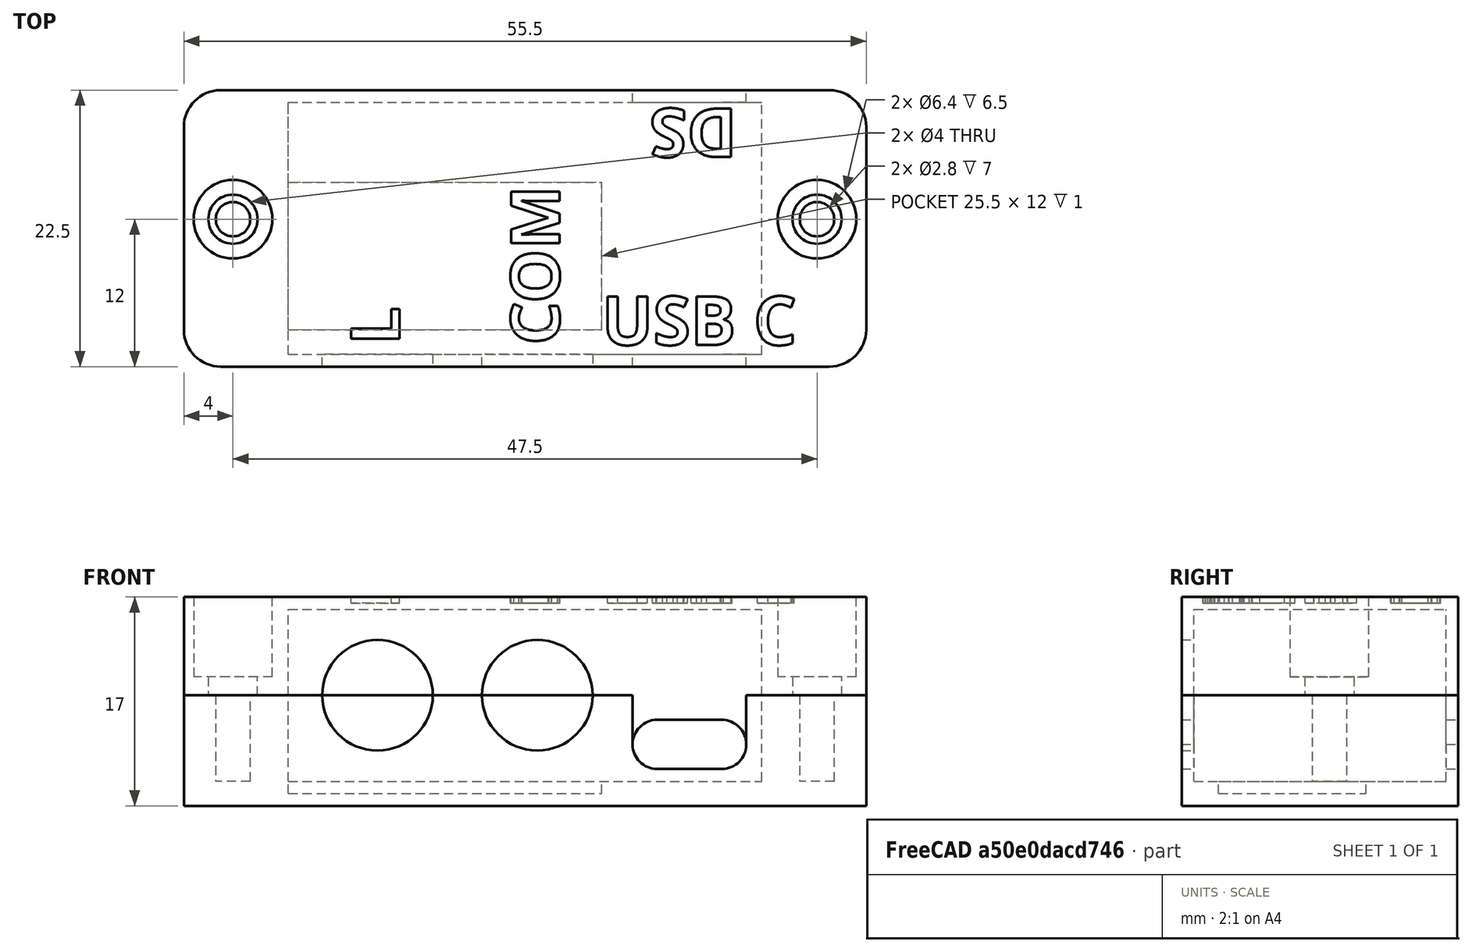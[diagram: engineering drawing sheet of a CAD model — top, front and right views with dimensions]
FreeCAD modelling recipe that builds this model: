
FCSTD DOCUMENT  (FreeCAD 0.21R33771 (Git))
Label: ds_lite_macro_tv_out_box
License: All rights reserved
LicenseURL: https://en.wikipedia.org/wiki/All_rights_reserved
objects: Part::Box×11, Part::Cylinder×10, Part::Fillet×6, Part::Cut×6, Part::MultiFuse×5, Part::Part2DObjectPython×4, Part::Extrusion×4
note: 46 computed .brp shape members not serialized (recipe doc carries the construction recipe); baked Part::Feature solids carry a one-line shape summary decoded from their .brp

FEATURE [Part::Box] Box  label="Cube(inner_base)"
  AttacherType = Attacher::AttachEngine3D
  Height = 7
  Length = 38.5
  Width = 20.5
FEATURE [Part::Box] Box001  label="Cube001(usb_c_charging)"
  AttacherType = Attacher::AttachEngine3D
  Height = 7
  Length = 9.25
  Placement = pos=(28,-1,1) rot=(0,0,1;0rad)
  Width = 1
FEATURE [Part::Cylinder] Cylinder  label="Cylinder(com_port_base)"
  Angle = 360
  AttacherType = Attacher::AttachEngine3D
  FirstAngle = 0
  Height = 1
  Placement = pos=(20.25,0,7) rot=(1,0,0;1.5708rad)
  Radius = 4.5
  SecondAngle = 0
FEATURE [Part::Box] Box002  label="Cube(outer_base)"
  AttacherType = Attacher::AttachEngine3D
  Height = 9
  Length = 55.5
  Placement = pos=(-8.5,-1,-2) rot=(0,0,1;0rad)
  Width = 22.5
FEATURE [Part::Cylinder] Cylinder001  label="Cylinder(L_port_base)"
  Angle = 360
  AttacherType = Attacher::AttachEngine3D
  FirstAngle = 0
  Height = 1
  Placement = pos=(7.25,0,7) rot=(1,0,0;1.5708rad)
  Radius = 4.5
  SecondAngle = 0
FEATURE [Part::Box] Box003  label="Cube001(usb_c_ds_side)"
  AttacherType = Attacher::AttachEngine3D
  Height = 7
  Length = 9.25
  Placement = pos=(28,20.5,1) rot=(0,0,1;0rad)
  Width = 1
FEATURE [Part::Fillet] Fillet  label="Fillet(usb_c_charging_base)"
  Base = -> Box001
  Edges = 2 edges r=2: [Edge4,Edge8]
FEATURE [Part::Fillet] Fillet001  label="Fillet001(usb_c_ds_side_base)"
  Base = -> Box003
  Edges = 2 edges r=2: [Edge4,Edge8]
FEATURE [Part::Box] Box004  label="Cube(inner_lid)"
  AttacherType = Attacher::AttachEngine3D
  Height = 7
  Length = 38.5
  Placement = pos=(0,0,7) rot=(0,0,1;0rad)
  Width = 20.5
FEATURE [Part::Box] Box005  label="Cube(outer_lid)"
  AttacherType = Attacher::AttachEngine3D
  Height = 8
  Length = 55.5
  Placement = pos=(-8.5,-1,7) rot=(0,0,1;0rad)
  Width = 22.5
FEATURE [Part::Box] Box006  label="Cube(inner_base_cutout)"
  AttacherType = Attacher::AttachEngine3D
  Height = 1
  Length = 25.5
  Placement = pos=(0,2,-1) rot=(0,0,1;0rad)
  Width = 12
FEATURE [Part::Box] Box007  label="Cube001(usb_c_charging_lid)"
  AttacherType = Attacher::AttachEngine3D
  Height = 4.5
  Length = 9.25
  Placement = pos=(28,-1,2.5) rot=(0,0,1;0rad)
  Width = 1
FEATURE [Part::Box] Box008  label="Cube001(usb_c_ds_side_lid)"
  AttacherType = Attacher::AttachEngine3D
  Height = 4.5
  Length = 9.25
  Placement = pos=(28,20.5,2.5) rot=(0,0,1;0rad)
  Width = 1
FEATURE [Part::Cylinder] Cylinder002  label="Cylinder(L_port_lid)"
  Angle = 360
  AttacherType = Attacher::AttachEngine3D
  FirstAngle = 0
  Height = 1
  Placement = pos=(7.25,0,7) rot=(1,0,0;1.5708rad)
  Radius = 4.5
  SecondAngle = 0
FEATURE [Part::Cylinder] Cylinder003  label="Cylinder(com_port_lid)"
  Angle = 360
  AttacherType = Attacher::AttachEngine3D
  FirstAngle = 0
  Height = 1
  Placement = pos=(20.25,0,7) rot=(1,0,0;1.5708rad)
  Radius = 4.5
  SecondAngle = 0
FEATURE [Part::MultiFuse] Fusion
  Shapes = -> [Box,Cylinder,Cylinder001,Fillet,Fillet001,Box006]
FEATURE [Part::Cut] Cut  label="Cut(base)"
  Base = -> Box002
  Tool = -> Fusion
FEATURE [Part::Box] Box009  label="Cube001(usb_c_charging_lid)001"
  AttacherType = Attacher::AttachEngine3D
  Height = 2.5
  Length = 9.25
  Placement = pos=(28,-1,2.5) rot=(0,0,1;0rad)
  Width = 1
FEATURE [Part::Fillet] Fillet002
  Base = -> Box009
  Edges = 2 edges r=2: [Edge2,Edge6]
FEATURE [Part::Cut] Cut001
  Base = -> Box007
  Tool = -> Fillet002
FEATURE [Part::Box] Box010  label="Cube001(usb_c_ds_side_lid)001"
  AttacherType = Attacher::AttachEngine3D
  Height = 2.5
  Length = 9.25
  Placement = pos=(28,20.5,2.5) rot=(0,0,1;0rad)
  Width = 1
FEATURE [Part::Fillet] Fillet003
  Base = -> Box010
  Edges = 2 edges r=2: [Edge2,Edge6]
FEATURE [Part::Cut] Cut002
  Base = -> Box008
  Tool = -> Fillet003
FEATURE [Part::Cylinder] Cylinder004  label="Cylinder(bolt_head_clear_left)"
  Angle = 360
  AttacherType = Attacher::AttachEngine3D
  FirstAngle = 0
  Height = 6.5
  Placement = pos=(-4.5,11,8.5) rot=(0,0,1;0rad)
  Radius = 3.2
  SecondAngle = 0
FEATURE [Part::Cylinder] Cylinder005  label="Cylinder(bolt_thread_left)"
  Angle = 360
  AttacherType = Attacher::AttachEngine3D
  FirstAngle = 0
  Height = 7
  Placement = pos=(-4.5,11,0) rot=(0,0,1;0rad)
  Radius = 1.4
  SecondAngle = 0
FEATURE [Part::Cylinder] Cylinder006  label="Cylinder(bolt_clear_left)"
  Angle = 360
  AttacherType = Attacher::AttachEngine3D
  FirstAngle = 0
  Height = 1.5
  Placement = pos=(-4.5,11,7) rot=(0,0,1;0rad)
  Radius = 2
  SecondAngle = 0
FEATURE [Part::Cylinder] Cylinder007  label="Cylinder(bolt_head_clear_right)"
  Angle = 360
  AttacherType = Attacher::AttachEngine3D
  FirstAngle = 0
  Height = 6.5
  Placement = pos=(43,11,8.5) rot=(0,0,1;0rad)
  Radius = 3.2
  SecondAngle = 0
FEATURE [Part::Cylinder] Cylinder008  label="Cylinder(bolt_thread_right)"
  Angle = 360
  AttacherType = Attacher::AttachEngine3D
  FirstAngle = 0
  Height = 7
  Placement = pos=(43,11,0) rot=(0,0,1;0rad)
  Radius = 1.4
  SecondAngle = 0
FEATURE [Part::Cylinder] Cylinder009  label="Cylinder(bolt_clear_right)"
  Angle = 360
  AttacherType = Attacher::AttachEngine3D
  FirstAngle = 0
  Height = 1.5
  Placement = pos=(43,11,7) rot=(0,0,1;0rad)
  Radius = 2
  SecondAngle = 0
FEATURE [Part::Fillet] Fillet004
  Base = -> Box005
  Edges = 4 edges r=3: [Edge1,Edge3,Edge5,Edge7]
FEATURE [Part::Part2DObjectPython] ShapeString  # Draft 2D object (typed FeaturePython)
  FontFile = <userpath>/stuff/3dprinting/fonts/open-sans/OpenSans-Bold.ttf
  MakeFace = true
  Placement = pos=(22.05,0.77,14.5) rot=(0,0,1;1.5708rad)
  Size = 5
  String = COM
  Tracking = 0
FEATURE [Part::Part2DObjectPython] ShapeString001  # Draft 2D object (typed FeaturePython)
  FontFile = <userpath>/stuff/3dprinting/fonts/open-sans/OpenSans-Bold.ttf
  MakeFace = true
  Placement = pos=(9.05,0.77,14.5) rot=(0,0,1;1.5708rad)
  Size = 5
  String = L
  Tracking = 0
FEATURE [Part::Part2DObjectPython] ShapeString002  # Draft 2D object (typed FeaturePython)
  FontFile = <userpath>/stuff/3dprinting/fonts/open-sans/OpenSans-Bold.ttf
  MakeFace = true
  Placement = pos=(36.5,20,14.5) rot=(0,0,1;3.14159rad)
  Size = 5
  String = DS
  Tracking = 0
FEATURE [Part::Part2DObjectPython] ShapeString003  # Draft 2D object (typed FeaturePython)
  FontFile = <userpath>/stuff/3dprinting/fonts/open-sans/OpenSans-Bold.ttf
  MakeFace = true
  Placement = pos=(25.5,0.77,14.5) rot=(0,0,1;0rad)
  Size = 5
  String = USB C
  Tracking = 0
FEATURE [Part::Extrusion] Extrude
  Base = -> ShapeString
  Dir = (0,0,1)
  DirMode = 2
  FaceMakerClass = Part::FaceMakerBullseye
  LengthFwd = 0.5
  LengthRev = 0
  Solid = false
  Symmetric = false
FEATURE [Part::Extrusion] Extrude001
  Base = -> ShapeString001
  Dir = (0,0,1)
  DirMode = 2
  FaceMakerClass = Part::FaceMakerBullseye
  LengthFwd = 0.5
  LengthRev = 0
  Solid = false
  Symmetric = false
FEATURE [Part::Extrusion] Extrude002
  Base = -> ShapeString002
  Dir = (0,0,1)
  DirMode = 2
  FaceMakerClass = Part::FaceMakerBullseye
  LengthFwd = 0.5
  LengthRev = 0
  Solid = false
  Symmetric = false
FEATURE [Part::Extrusion] Extrude003
  Base = -> ShapeString003
  Dir = (0,0,1)
  DirMode = 2
  FaceMakerClass = Part::FaceMakerBullseye
  LengthFwd = 0.5
  LengthRev = 0
  Solid = false
  Symmetric = false
FEATURE [Part::MultiFuse] Fusion001
  Shapes = -> [Extrude,Extrude001,Extrude002,Extrude003]
FEATURE [Part::MultiFuse] Fusion002
  Shapes = -> [Cylinder005,Cylinder008]
FEATURE [Part::Cut] Cut003
  Base = -> Cut
  Tool = -> Fusion002
FEATURE [Part::Fillet] Fillet005  label="Fillet005(base)"
  Base = -> Cut003
  Edges = 4 edges r=3: [Edge1,Edge3,Edge5,Edge25]
FEATURE [Part::MultiFuse] Fusion003
  Shapes = -> [Cylinder009,Cylinder007,Cylinder006,Cylinder004,Cylinder003,Cylinder002,Box004]
FEATURE [Part::MultiFuse] Fusion004
  Shapes = -> [Fillet004,Cut001,Cut002]
FEATURE [Part::Cut] Cut004
  Base = -> Fusion004
  Tool = -> Fusion003
FEATURE [Part::Cut] Cut005  label="Cut005(lid)"
  Base = -> Cut004
  Tool = -> Fusion001
